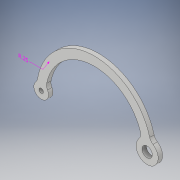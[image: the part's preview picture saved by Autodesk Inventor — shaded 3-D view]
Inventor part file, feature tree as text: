
AUTODESK INVENTOR PART (.ipt)
format: ipt  version: 2018 (Build 220112000, 112)  size: 141,312 bytes
history: native  units: in
note: dims shown in document units (in); Inventor stores cm internally (conversion verified against a paired STEP export)
features: other x2, extrude x2, sketch x2
ambient origin geometry x8: Origin, YZ Plane, XZ Plane, XY Plane, X Axis, Y Axis, Z Axis, Center Point
bodies: Solid1 (feature_tree)
feature tree (6):
  other  "Annotations"
  extrude  "Extrusion1"  Depth=0.1181in
  extrude  "Extrusion11"  Depth=0.1969in
  sketch  "Sketch1"  dims[d7=0.1181in d8=0.0in d15=1.0in]
  sketch  "Sketch12"  dims[d47=0.1969in d48=0.1969in d63=2.1654in d64=0.1969in d70=0.2756in d72=0.1969in d73=0.0in d79=2.8346in d82=0.1181in d83=0.1181in d84=0.1181in d85=0.3937in d86=0.5906in d87=0.1969in d28=1.2193in d29=0.25in]
  other  "Radial Dimension 1"
